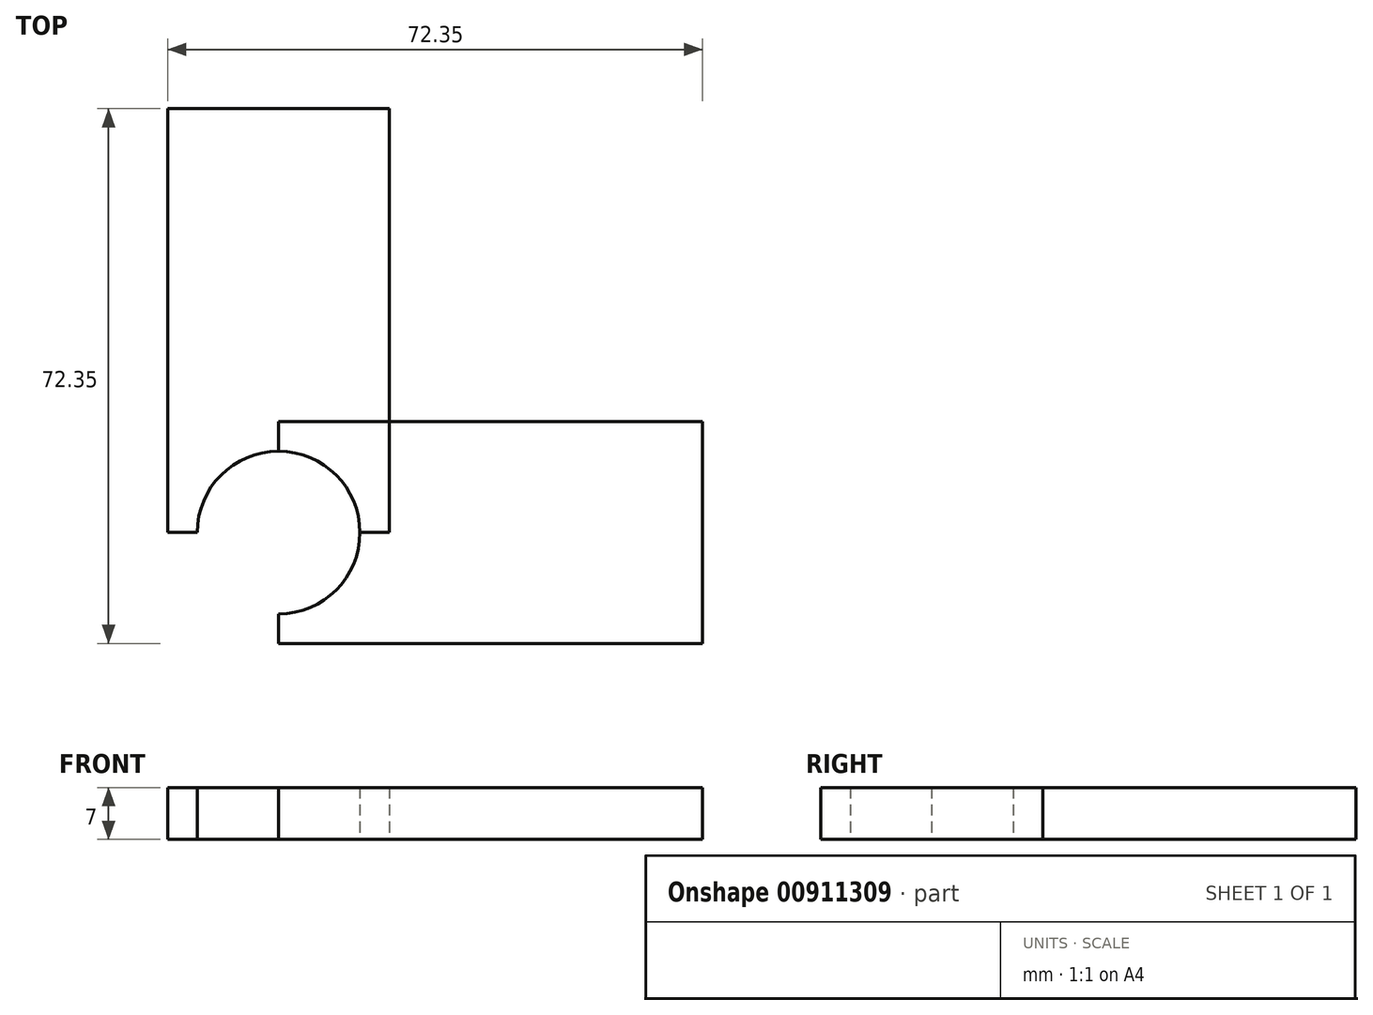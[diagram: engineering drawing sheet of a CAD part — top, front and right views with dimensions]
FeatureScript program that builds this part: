
annotation { "Feature Type Name" : "Feature", "Feature Type Description" : "" }
export const myFeature = defineFeature(function(context is Context, id is Id, definition is map)
    precondition{}
    {
        {
            var Q0;
            Q0=qCreatedBy(makeId("Top.planeOp"),FACE);
            var sketch = newSketch(context, id + "F0", { "sketchPlane" : qUnion([Q0])});
            skCircle(sketch, "E0", {"center": v(0, 0) * mm, "radius": 11 * mm});
            skLineSegment(sketch, "E1", {"start": v(0, 0) * mm, "end": v(0, 57.35) * mm});
            skLineSegment(sketch, "E2", {"start": v(0, 57.35) * mm, "end": v(15, 57.35) * mm});
            skLineSegment(sketch, "E3", {"start": v(15, 57.35) * mm, "end": v(15, 0) * mm});
            skLineSegment(sketch, "E4", {"start": v(15, 0) * mm, "end": v(0, 0) * mm});
            skLineSegment(sketch, "E5", {"start": v(0, 0) * mm, "end": v(-15, 0) * mm});
            skLineSegment(sketch, "E6", {"start": v(-15, 0) * mm, "end": v(-15, 57.35) * mm});
            skLineSegment(sketch, "E7", {"start": v(-15, 57.35) * mm, "end": v(0, 57.35) * mm});
            skLineSegment(sketch, "E8", {"start": v(0, 0) * mm, "end": v(15, 0) * mm});
            skLineSegment(sketch, "E9", {"start": v(15, 0) * mm, "end": v(15, -55.46) * mm});
            skLineSegment(sketch, "E10", {"start": v(15, -55.46) * mm, "end": v(0, -55.46) * mm});
            skLineSegment(sketch, "E11", {"start": v(0, -55.46) * mm, "end": v(0, 0) * mm});
            skLineSegment(sketch, "E12", {"start": v(-15, 0) * mm, "end": v(-15, -56.03) * mm});
            skLineSegment(sketch, "E13", {"start": v(-15, -56.03) * mm, "end": v(0, -55.46) * mm});
            skSolve(sketch);
        }
        {
            var Q0;
            {var subQ1=sQuery(id+"F0.wireOp",EDGE,"E6");Q0=makeQuery(id+"F0.imprint","IMPRINT",FACE,{"disambiguationData":[TD([[makeQuery(id+"F0.imprint","IMPRINT",EDGE,{"derivedFrom":subQ1}),-1.0]])]});}
            var Q1;
            {var subQ1=sQuery(id+"F0.wireOp",EDGE,"E2");Q1=makeQuery(id+"F0.imprint","IMPRINT",FACE,{"disambiguationData":[TD([[makeQuery(id+"F0.imprint","IMPRINT",EDGE,{"derivedFrom":subQ1}),-1.0]])]});}
            extrude(context, id + "F1", {"entities" : qUnion([Q0, Q1]), "depth" : 7 * mm, "offsetDistance" : 25 * mm});
        }
        {
            var Q0;
            Q0=qCreatedBy(makeId("Front.planeOp"),FACE);
            var sketch = newSketch(context, id + "F2", { "sketchPlane" : qUnion([Q0])});
            skLineSegment(sketch, "E14", {"start": v(0, 0) * mm, "end": v(0, -78.05) * mm});
            skSolve(sketch);
        }
        {
            var Q0;
            Q0=makeQuery(id+"F1.opExtrude","SWEPT_BODY",BODY,{"disambiguationData":[OSD([sQuery(id+"F0.wireOp",EDGE,"E0"),sQuery(id+"F0.wireOp",EDGE,"E2"),sQuery(id+"F0.wireOp",EDGE,"E3"),sQuery(id+"F0.wireOp",EDGE,"E6"),sQuery(id+"F0.wireOp",EDGE,"E7"),sQuery(id+"F0.wireOp",EDGE,"E8"),sQuery(id+"F0.wireOp",EDGE,"E5")])]});
            var Q1;
            Q1=sQuery(id+"F2.wireOp",EDGE,"E14");
            transform(context, id + "F3", {"entities" : qUnion([Q0]), "transformType" : TransformType.ROTATION, "transformAxis" : qUnion([Q1]), "angle" : 90 * degree, "makeCopy" : true});
        }
    });
